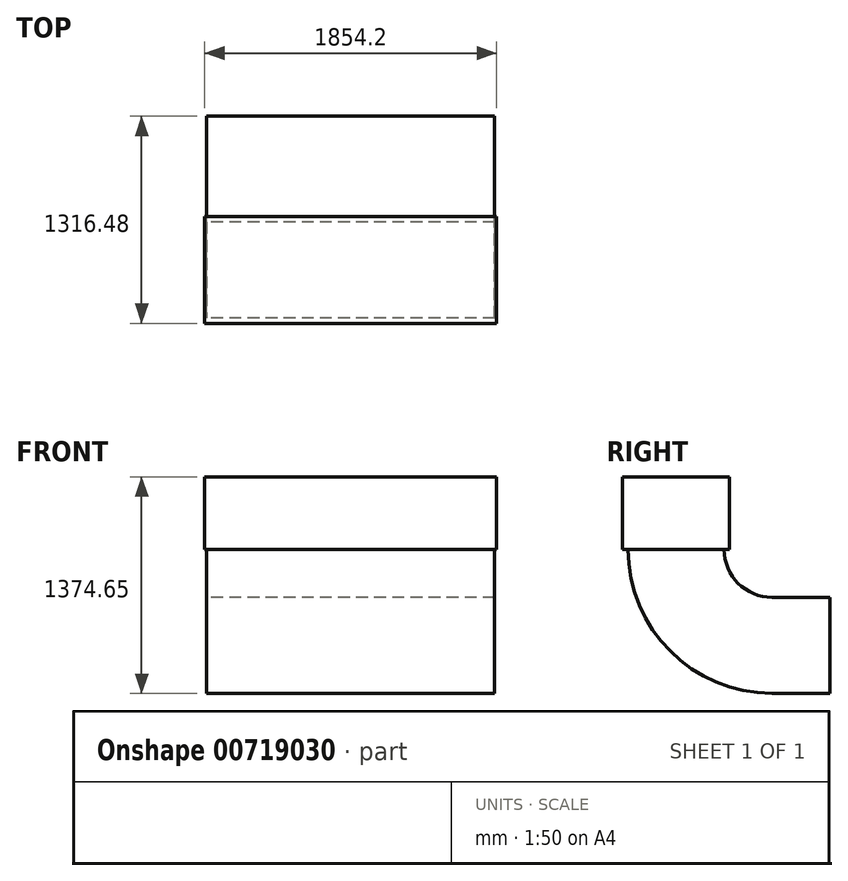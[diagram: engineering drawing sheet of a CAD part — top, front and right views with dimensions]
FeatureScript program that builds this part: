
annotation { "Feature Type Name" : "Feature", "Feature Type Description" : "" }
export const myFeature = defineFeature(function(context is Context, id is Id, definition is map)
    precondition{}
    {
        {
            var Q0;
            Q0=qCreatedBy(makeId("Front.planeOp"),FACE);
            var sketch = newSketch(context, id + "F0", { "sketchPlane" : qUnion([Q0])});
            skLineSegment(sketch, "E0.bottom", {"start": v(914.4, 304.8) * mm, "end": v(-914.4, 304.8) * mm});
            skLineSegment(sketch, "E0.top", {"start": v(914.4, -304.8) * mm, "end": v(-914.4, -304.8) * mm});
            skLineSegment(sketch, "E0.left", {"start": v(914.4, 304.8) * mm, "end": v(914.4, -304.8) * mm});
            skLineSegment(sketch, "E0.right", {"start": v(-914.4, 304.8) * mm, "end": v(-914.4, -304.8) * mm});
            skPoint(sketch, "E0.middle", {"position": v(0, 0) * mm});
            skSolve(sketch);
        }
        {
            var Q0;
            Q0=makeQuery(id+"F0.imprint","IMPRINT",FACE,{"disambiguationData":[TD([[makeQuery(id+"F0.imprint","IMPRINT",EDGE,{"derivedFrom":sQuery(id+"F0.wireOp",EDGE,"E0.bottom")}),1.0]])]});
            var sketch = newSketch(context, id + "F1", { "sketchPlane" : qUnion([Q0])});
            skLineSegment(sketch, "E1", {"start": v(0, 0) * mm, "end": v(0, 609.6) * mm, "construction": true});
            skLineSegment(sketch, "E2", {"start": v(0, 609.6) * mm, "end": v(-398.2, 609.6) * mm});
            skSolve(sketch);
        }
        {
            var Q0;
            Q0=makeQuery(id+"F0.imprint","IMPRINT",FACE,{"disambiguationData":[TD([[makeQuery(id+"F0.imprint","IMPRINT",EDGE,{"derivedFrom":sQuery(id+"F0.wireOp",EDGE,"E0.bottom")}),1.0]])]});
            var Q1;
            Q1=sQuery(id+"F1.wireOp",EDGE,"E2");
            revolve(context, id + "F2", {"surfaceOperationType" : NewSurfaceOperationType.NEW, "entities" : qUnion([Q0]), "axis" : qUnion([Q1]), "revolveType" : RevolveType.ONE_DIRECTION, "angle" : 90 * degree});
        }
        {
            var Q0;
            Q0=makeQuery(id+"F2.opRevolve","CAP_FACE",FACE,{"disambiguationData":[OSD([sQuery(id+"F0.wireOp",EDGE,"E0.bottom"),sQuery(id+"F0.wireOp",EDGE,"E0.top"),sQuery(id+"F0.wireOp",EDGE,"E0.left"),sQuery(id+"F0.wireOp",EDGE,"E0.right")])],"isStart":true});
            extrude(context, id + "F3", {"entities" : qUnion([Q0]), "operationType" : NewBodyOperationType.ADD, "depth" : 367.28 * mm, "offsetDistance" : 25.4 * mm});
        }
        {
            var Q0;
            Q0=makeQuery(id+"F2.opRevolve","CAP_FACE",FACE,{"disambiguationData":[OSD([sQuery(id+"F0.wireOp",EDGE,"E0.bottom"),sQuery(id+"F0.wireOp",EDGE,"E0.top"),sQuery(id+"F0.wireOp",EDGE,"E0.left"),sQuery(id+"F0.wireOp",EDGE,"E0.right")])],"isStart":false});
            var sketch = newSketch(context, id + "F4", { "sketchPlane" : qUnion([Q0])});
            skLineSegment(sketch, "E3.bottom", {"start": v(927.1, -270) * mm, "end": v(-927.1, -270) * mm});
            skLineSegment(sketch, "E3.top", {"start": v(927.1, -949.2) * mm, "end": v(-927.1, -949.2) * mm});
            skLineSegment(sketch, "E3.left", {"start": v(927.1, -270) * mm, "end": v(927.1, -949.2) * mm});
            skLineSegment(sketch, "E3.right", {"start": v(-927.1, -270) * mm, "end": v(-927.1, -949.2) * mm});
            skPoint(sketch, "E3.middle", {"position": v(0, -609.6) * mm});
            skPoint(sketch, "E3.middle.positionSnap0", {"position": v(0, -304.8) * mm});
            skPoint(sketch, "E3.middle.positionSnap1", {"position": v(-914.4, -609.6) * mm});
            skPoint(sketch, "E3.centerSnap0", {"position": v(0, -304.8) * mm});
            skPoint(sketch, "E3.centerSnap1", {"position": v(-914.4, -609.6) * mm});
            skSolve(sketch);
        }
        {
            var Q0;
            Q0 = qSketchRegion(id + "F4", true);
            extrude(context, id + "F5", {"entities" : qUnion([Q0]), "operationType" : NewBodyOperationType.ADD, "depth" : 460.25 * mm, "offsetDistance" : 25.4 * mm});
        }
    });
